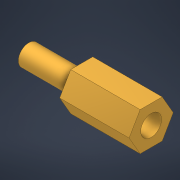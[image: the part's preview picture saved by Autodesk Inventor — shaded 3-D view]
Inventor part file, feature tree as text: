
AUTODESK INVENTOR PART (.ipt)
format: ipt  version: 2022 (Build 260153000, 153)  size: 108,544 bytes
history: native  units: in
note: dims shown in document units (in); Inventor stores cm internally (conversion verified against a paired STEP export)
features: extrude x3, sketch x3
ambient origin geometry x8: Origin, YZ Plane, XZ Plane, XY Plane, X Axis, Y Axis, Z Axis, Center Point
bodies: Solid1 (feature_tree)
feature tree (6):
  extrude  "Extrusion1"  Depth=0.3937in TaperAngle=0.0deg
  extrude  "Extrusion2"  Depth=0.3in TaperAngle=0.0deg
  extrude  "Extrusion3"  Depth=0.2362in TaperAngle=0.0deg
  sketch  "Sketch1"  dims[d1=0.2165in d2=0.3937in d3=0.0in]
  sketch  "Sketch2"  dims[d4=0.1181in d5=0.3in d6=0.0in]
  sketch  "Sketch3"  dims[d7=0.1181in d8=0.2362in d9=0.0in]
